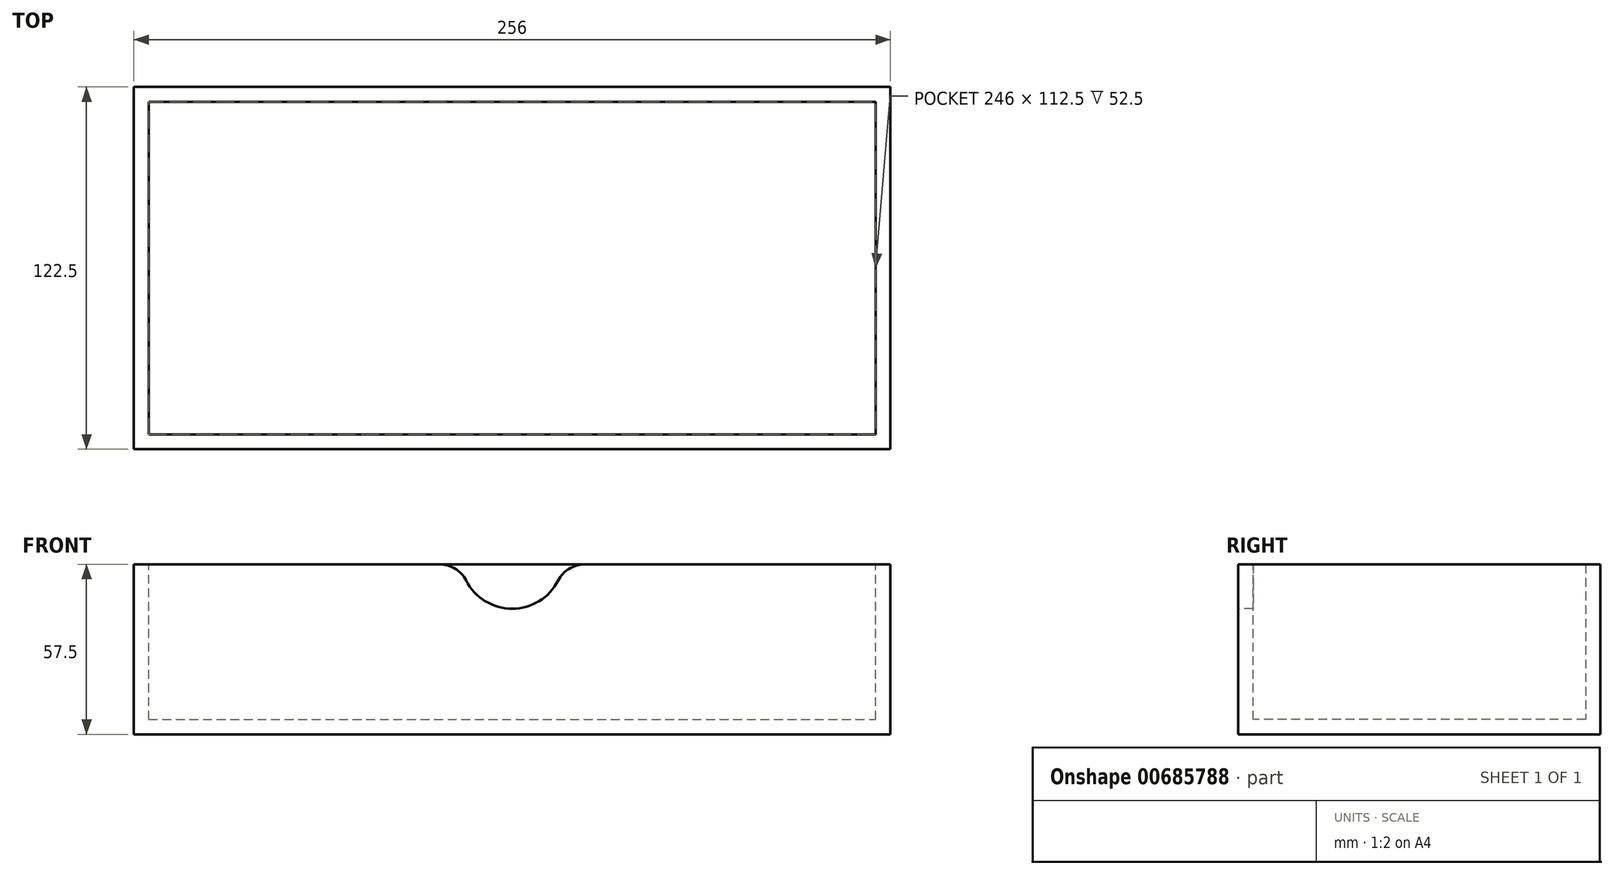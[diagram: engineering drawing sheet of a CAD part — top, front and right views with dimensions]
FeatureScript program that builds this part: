
annotation { "Feature Type Name" : "Feature", "Feature Type Description" : "" }
export const myFeature = defineFeature(function(context is Context, id is Id, definition is map)
    precondition{}
    {
        {
            var Q0;
            Q0=qCreatedBy(makeId("Front.planeOp"),FACE);
            var sketch = newSketch(context, id + "F0", { "sketchPlane" : qUnion([Q0])});
            skLineSegment(sketch, "E0.bottom", {"start": v(0, 0) * mm, "end": v(256, 0) * mm});
            skLineSegment(sketch, "E0.top", {"start": v(0, 57.5) * mm, "end": v(256, 57.5) * mm});
            skLineSegment(sketch, "E0.left", {"start": v(0, 0) * mm, "end": v(0, 57.5) * mm});
            skLineSegment(sketch, "E0.right", {"start": v(256, 0) * mm, "end": v(256, 57.5) * mm});
            skSolve(sketch);
        }
        {
            var Q0;
            Q0 = qSketchRegion(id + "F0", true);
            extrude(context, id + "F1", {"entities" : qUnion([Q0]), "depth" : 2.5 * mm, "offsetDistance" : 25 * mm});
        }
        {
            var Q0;
            Q0=makeQuery(id+"F1.opExtrude","CAP_FACE",FACE,{"disambiguationData":[OSD([sQuery(id+"F0.wireOp",EDGE,"E0.bottom"),sQuery(id+"F0.wireOp",EDGE,"E0.top"),sQuery(id+"F0.wireOp",EDGE,"E0.left"),sQuery(id+"F0.wireOp",EDGE,"E0.right")])],"isStart":true});
            var sketch = newSketch(context, id + "F2", { "sketchPlane" : qUnion([Q0])});
            skLineSegment(sketch, "E1.0", {"start": v(-251, 2.5) * mm, "end": v(-251, 57.5) * mm});
            skLineSegment(sketch, "E1.1", {"start": v(-5, 2.5) * mm, "end": v(-251, 2.5) * mm});
            skLineSegment(sketch, "E1.2", {"start": v(-5, 2.5) * mm, "end": v(-5, 57.5) * mm});
            skLineSegment(sketch, "E2", {"start": v(-251, 57.5) * mm, "end": v(-5, 57.5) * mm});
            skSolve(sketch);
        }
        {
            var Q0;
            Q0 = qSketchRegion(id + "F2", true);
            extrude(context, id + "F3", {"entities" : qUnion([Q0]), "operationType" : NewBodyOperationType.ADD, "depth" : 2.5 * mm, "offsetDistance" : 25 * mm});
        }
        {
            var Q0;
            Q0=makeQuery(id+"F1.opExtrude","CAP_FACE",FACE,{"disambiguationData":[OSD([sQuery(id+"F0.wireOp",EDGE,"E0.bottom"),sQuery(id+"F0.wireOp",EDGE,"E0.top"),sQuery(id+"F0.wireOp",EDGE,"E0.left"),sQuery(id+"F0.wireOp",EDGE,"E0.right")])],"isStart":false});
            var sketch = newSketch(context, id + "F4", { "sketchPlane" : qUnion([Q0])});
            skCircle(sketch, "E3", {"center": v(128, 60) * mm, "radius": 17.5 * mm});
            skPoint(sketch, "E3.centerSnap0", {"position": v(128, 57.5) * mm});
            skSolve(sketch);
        }
        {
            var Q0;
            Q0 = qSketchRegion(id + "F4", true);
            extrude(context, id + "F5", {"entities" : qUnion([Q0]), "operationType" : NewBodyOperationType.REMOVE, "oppositeDirection" : true, "depth" : 25 * mm, "offsetDistance" : 25 * mm});
        }
        {
            var Q0;
            Q0=makeQuery(id+"F5.boolean.opBoolean","INTERSECT",EDGE,{"disambiguationData":[OD(0.0)],"derivedFrom":[makeQuery(id+"F3.boolean.opBoolean","MERGE",FACE,{"derivedFrom":[makeQuery(id+"F1.opExtrude","SWEPT_FACE",FACE,{"disambiguationData":[OSD([sQuery(id+"F0.wireOp",EDGE,"E0.top")])]}),makeQuery(id+"F3.opExtrude","SWEPT_FACE",FACE,{"disambiguationData":[OSD([sQuery(id+"F2.wireOp",EDGE,"E2")])]})]}),makeQuery(id+"F5.opExtrude","SWEPT_FACE",FACE,{"disambiguationData":[OSD([sQuery(id+"F4.wireOp",EDGE,"E3")])]})]});
            var Q1;
            Q1=makeQuery(id+"F5.boolean.opBoolean","INTERSECT",EDGE,{"disambiguationData":[OD(1.0)],"derivedFrom":[makeQuery(id+"F3.boolean.opBoolean","MERGE",FACE,{"derivedFrom":[makeQuery(id+"F1.opExtrude","SWEPT_FACE",FACE,{"disambiguationData":[OSD([sQuery(id+"F0.wireOp",EDGE,"E0.top")])]}),makeQuery(id+"F3.opExtrude","SWEPT_FACE",FACE,{"disambiguationData":[OSD([sQuery(id+"F2.wireOp",EDGE,"E2")])]})]}),makeQuery(id+"F5.opExtrude","SWEPT_FACE",FACE,{"disambiguationData":[OSD([sQuery(id+"F4.wireOp",EDGE,"E3")])]})]});
            fillet(context, id + "F6", {"entities" : qUnion([Q0, Q1]), "radius" : 10 * mm, "tangentPropagation" : true, "allowEdgeOverflow" : false});
        }
        {
            var Q0;
            Q0=makeQuery(id+"F1.opExtrude","SWEPT_FACE",FACE,{"disambiguationData":[OSD([sQuery(id+"F0.wireOp",EDGE,"E0.right")])]});
            var sketch = newSketch(context, id + "F7", { "sketchPlane" : qUnion([Q0])});
            skLineSegment(sketch, "E4.bottom", {"start": v(0, 57.5) * mm, "end": v(117.5, 57.5) * mm});
            skLineSegment(sketch, "E4.top", {"start": v(0, 2.5) * mm, "end": v(117.5, 2.5) * mm});
            skLineSegment(sketch, "E4.left", {"start": v(0, 57.5) * mm, "end": v(0, 2.5) * mm});
            skLineSegment(sketch, "E4.right", {"start": v(117.5, 57.5) * mm, "end": v(117.5, 2.5) * mm});
            skSolve(sketch);
        }
        {
            var Q0;
            Q0 = qSketchRegion(id + "F7", true);
            extrude(context, id + "F8", {"entities" : qUnion([Q0]), "oppositeDirection" : true, "depth" : 5 * mm, "offsetDistance" : 25 * mm});
        }
        {
            var Q0;
            Q0=makeQuery(id+"F8.opExtrude","SWEPT_BODY",BODY,{"disambiguationData":[OSD([sQuery(id+"F7.wireOp",EDGE,"E4.bottom"),sQuery(id+"F7.wireOp",EDGE,"E4.top"),sQuery(id+"F7.wireOp",EDGE,"E4.left"),sQuery(id+"F7.wireOp",EDGE,"E4.right")])]});
            transform(context, id + "F9", {"entities" : qUnion([Q0]), "transformType" : TransformType.TRANSLATION_3D, "dx" : -251 * mm, "dy" : 0 * mm, "dz" : 0 * mm, "makeCopy" : true});
        }
        {
            var Q0;
            Q0=makeQuery(id+"F8.opExtrude","SWEPT_FACE",FACE,{"disambiguationData":[OSD([sQuery(id+"F7.wireOp",EDGE,"E4.right")])]});
            var sketch = newSketch(context, id + "F10", { "sketchPlane" : qUnion([Q0])});
            skLineSegment(sketch, "E5.bottom", {"start": v(-256, 57.5) * mm, "end": v(0, 57.5) * mm});
            skLineSegment(sketch, "E5.top", {"start": v(-256, 0) * mm, "end": v(0, 0) * mm});
            skLineSegment(sketch, "E5.left", {"start": v(-256, 57.5) * mm, "end": v(-256, 0) * mm});
            skLineSegment(sketch, "E5.right", {"start": v(0, 57.5) * mm, "end": v(0, 0) * mm});
            skSolve(sketch);
        }
        {
            var Q0;
            Q0 = qSketchRegion(id + "F10", true);
            extrude(context, id + "F11", {"entities" : qUnion([Q0]), "depth" : 2.5 * mm, "offsetDistance" : 25 * mm});
        }
        {
            var Q0;
            Q0=makeQuery(id+"F11.opExtrude","CAP_FACE",FACE,{"disambiguationData":[OSD([sQuery(id+"F10.wireOp",EDGE,"E5.bottom"),sQuery(id+"F10.wireOp",EDGE,"E5.top"),sQuery(id+"F10.wireOp",EDGE,"E5.left"),sQuery(id+"F10.wireOp",EDGE,"E5.right")])],"isStart":true});
            var sketch = newSketch(context, id + "F12", { "sketchPlane" : qUnion([Q0])});
            skLineSegment(sketch, "E6.bottom", {"start": v(5, 57.5) * mm, "end": v(251, 57.5) * mm});
            skLineSegment(sketch, "E6.top", {"start": v(5, 2.5) * mm, "end": v(251, 2.5) * mm});
            skLineSegment(sketch, "E6.left", {"start": v(5, 57.5) * mm, "end": v(5, 2.5) * mm});
            skLineSegment(sketch, "E6.right", {"start": v(251, 57.5) * mm, "end": v(251, 2.5) * mm});
            skSolve(sketch);
        }
        {
            var Q0;
            Q0 = qSketchRegion(id + "F12", true);
            extrude(context, id + "F13", {"entities" : qUnion([Q0]), "operationType" : NewBodyOperationType.ADD, "depth" : 2.5 * mm, "offsetDistance" : 25 * mm});
        }
        {
            var Q0;
            Q0=makeQuery(id+"F9.opPattern","COPY",FACE,{"derivedFrom":makeQuery(id+"F8.opExtrude","SWEPT_FACE",FACE,{"disambiguationData":[OSD([sQuery(id+"F7.wireOp",EDGE,"E4.top")])]}),"instanceName":"1"});
            var sketch = newSketch(context, id + "F14", { "sketchPlane" : qUnion([Q0])});
            skLineSegment(sketch, "E7.bottom", {"start": v(0, 0) * mm, "end": v(256, 0) * mm});
            skLineSegment(sketch, "E7.top", {"start": v(0, -117.5) * mm, "end": v(256, -117.5) * mm});
            skLineSegment(sketch, "E7.left", {"start": v(0, 0) * mm, "end": v(0, -117.5) * mm});
            skLineSegment(sketch, "E7.right", {"start": v(256, 0) * mm, "end": v(256, -117.5) * mm});
            skSolve(sketch);
        }
        {
            var Q0;
            Q0 = qSketchRegion(id + "F14", true);
            extrude(context, id + "F15", {"entities" : qUnion([Q0]), "depth" : 2.5 * mm, "offsetDistance" : 25 * mm});
        }
        {
            var Q0;
            Q0=makeQuery(id+"F15.opExtrude","CAP_FACE",FACE,{"disambiguationData":[OSD([sQuery(id+"F14.wireOp",EDGE,"E7.bottom"),sQuery(id+"F14.wireOp",EDGE,"E7.top"),sQuery(id+"F14.wireOp",EDGE,"E7.left"),sQuery(id+"F14.wireOp",EDGE,"E7.right")])],"isStart":true});
            var sketch = newSketch(context, id + "F16", { "sketchPlane" : qUnion([Q0])});
            skLineSegment(sketch, "E8.bottom", {"start": v(5, 115) * mm, "end": v(251, 115) * mm});
            skLineSegment(sketch, "E8.top", {"start": v(5, 2.5) * mm, "end": v(251, 2.5) * mm});
            skLineSegment(sketch, "E8.left", {"start": v(5, 115) * mm, "end": v(5, 2.5) * mm});
            skLineSegment(sketch, "E8.right", {"start": v(251, 115) * mm, "end": v(251, 2.5) * mm});
            skSolve(sketch);
        }
        {
            var Q0;
            Q0 = qSketchRegion(id + "F16", true);
            extrude(context, id + "F17", {"entities" : qUnion([Q0]), "operationType" : NewBodyOperationType.ADD, "depth" : 2.5 * mm, "offsetDistance" : 25 * mm});
        }
    });
